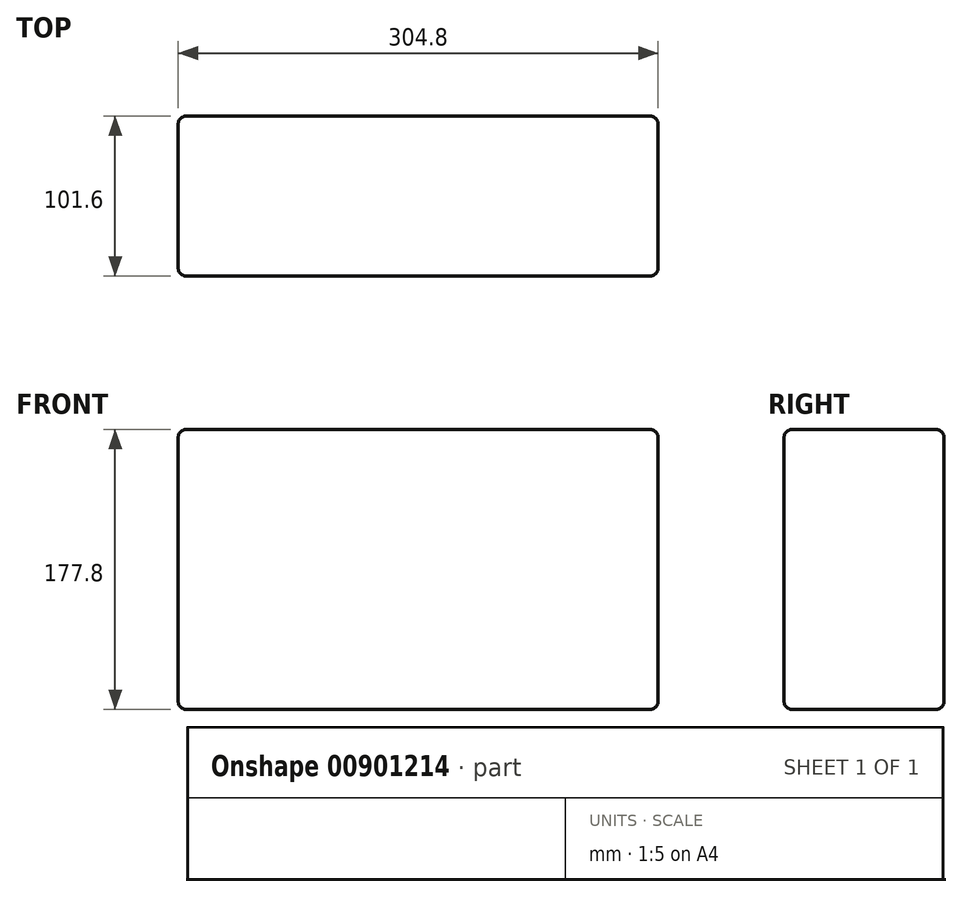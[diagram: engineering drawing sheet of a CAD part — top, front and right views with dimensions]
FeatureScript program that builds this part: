
annotation { "Feature Type Name" : "Feature", "Feature Type Description" : "" }
export const myFeature = defineFeature(function(context is Context, id is Id, definition is map)
    precondition{}
    {
        {
            var Q0;
            Q0=qCreatedBy(makeId("Front.planeOp"),FACE);
            var sketch = newSketch(context, id + "F0", { "sketchPlane" : qUnion([Q0])});
            skLineSegment(sketch, "E0.bottom", {"start": v(-304.8, 177.8) * mm, "end": v(0, 177.8) * mm});
            skLineSegment(sketch, "E0.top", {"start": v(-304.8, 0) * mm, "end": v(0, 0) * mm});
            skLineSegment(sketch, "E0.left", {"start": v(-304.8, 177.8) * mm, "end": v(-304.8, 0) * mm});
            skLineSegment(sketch, "E0.right", {"start": v(0, 177.8) * mm, "end": v(0, 0) * mm});
            skSolve(sketch);
        }
        {
            var Q0;
            Q0=makeQuery(id+"F0.imprint","IMPRINT",FACE,{"disambiguationData":[TD([[makeQuery(id+"F0.imprint","IMPRINT",EDGE,{"derivedFrom":sQuery(id+"F0.wireOp",EDGE,"E0.bottom")}),-1.0]])]});
            extrude(context, id + "F1", {"entities" : qUnion([Q0]), "depth" : 101.6 * mm, "offsetDistance" : 25.4 * mm});
        }
        {
            var Q0;
            Q0=makeQuery(id+"F1.opExtrude","SWEPT_EDGE",EDGE,{"disambiguationData":[OSD([sQuery(id+"F0.wireOp",EDGE,"E0.bottom"),sQuery(id+"F0.wireOp",EDGE,"E0.left")])]});
            var Q1;
            Q1=makeQuery(id+"F1.opExtrude","SWEPT_FACE",FACE,{"disambiguationData":[OSD([sQuery(id+"F0.wireOp",EDGE,"E0.bottom")])]});
            var Q2;
            Q2=makeQuery(id+"F1.opExtrude","SWEPT_EDGE",EDGE,{"disambiguationData":[OSD([sQuery(id+"F0.wireOp",EDGE,"E0.bottom"),sQuery(id+"F0.wireOp",EDGE,"E0.right")])]});
            var Q3;
            Q3=makeQuery(id+"F1.opExtrude","CAP_FACE",FACE,{"disambiguationData":[OSD([sQuery(id+"F0.wireOp",EDGE,"E0.bottom"),sQuery(id+"F0.wireOp",EDGE,"E0.top"),sQuery(id+"F0.wireOp",EDGE,"E0.left"),sQuery(id+"F0.wireOp",EDGE,"E0.right")])],"isStart":true});
            var Q4;
            Q4=makeQuery(id+"F1.opExtrude","CAP_FACE",FACE,{"disambiguationData":[OSD([sQuery(id+"F0.wireOp",EDGE,"E0.bottom"),sQuery(id+"F0.wireOp",EDGE,"E0.top"),sQuery(id+"F0.wireOp",EDGE,"E0.left"),sQuery(id+"F0.wireOp",EDGE,"E0.right")])],"isStart":false});
            var Q5;
            Q5=makeQuery(id+"F1.opExtrude","SWEPT_EDGE",EDGE,{"disambiguationData":[OSD([sQuery(id+"F0.wireOp",EDGE,"E0.top"),sQuery(id+"F0.wireOp",EDGE,"E0.right")])]});
            var Q6;
            Q6=makeQuery(id+"F1.opExtrude","SWEPT_FACE",FACE,{"disambiguationData":[OSD([sQuery(id+"F0.wireOp",EDGE,"E0.top")])]});
            var Q7;
            Q7=makeQuery(id+"F1.opExtrude","CAP_EDGE",EDGE,{"disambiguationData":[OSD([sQuery(id+"F0.wireOp",EDGE,"E0.bottom")])],"isStart":true});
            var Q8;
            Q8=makeQuery(id+"F1.opExtrude","CAP_EDGE",EDGE,{"disambiguationData":[OSD([sQuery(id+"F0.wireOp",EDGE,"E0.bottom")])],"isStart":false});
            var Q9;
            Q9=makeQuery(id+"F1.opExtrude","SWEPT_FACE",FACE,{"disambiguationData":[OSD([sQuery(id+"F0.wireOp",EDGE,"E0.right")])]});
            var Q10;
            Q10=makeQuery(id+"F1.opExtrude","CAP_EDGE",EDGE,{"disambiguationData":[OSD([sQuery(id+"F0.wireOp",EDGE,"E0.top")])],"isStart":false});
            var Q11;
            Q11=makeQuery(id+"F1.opExtrude","SWEPT_EDGE",EDGE,{"disambiguationData":[OSD([sQuery(id+"F0.wireOp",EDGE,"E0.top"),sQuery(id+"F0.wireOp",EDGE,"E0.left")])]});
            var Q12;
            Q12=makeQuery(id+"F1.opExtrude","SWEPT_FACE",FACE,{"disambiguationData":[OSD([sQuery(id+"F0.wireOp",EDGE,"E0.left")])]});
            var Q13;
            Q13=makeQuery(id+"F1.opExtrude","CAP_EDGE",EDGE,{"disambiguationData":[OSD([sQuery(id+"F0.wireOp",EDGE,"E0.top")])],"isStart":true});
            var Q14;
            Q14=makeQuery(id+"F1.opExtrude","CAP_EDGE",EDGE,{"disambiguationData":[OSD([sQuery(id+"F0.wireOp",EDGE,"E0.left")])],"isStart":true});
            var Q15;
            Q15=makeQuery(id+"F1.opExtrude","CAP_EDGE",EDGE,{"disambiguationData":[OSD([sQuery(id+"F0.wireOp",EDGE,"E0.left")])],"isStart":false});
            var Q16;
            Q16=makeQuery(id+"F1.opExtrude","CAP_EDGE",EDGE,{"disambiguationData":[OSD([sQuery(id+"F0.wireOp",EDGE,"E0.right")])],"isStart":true});
            var Q17;
            Q17=makeQuery(id+"F1.opExtrude","CAP_EDGE",EDGE,{"disambiguationData":[OSD([sQuery(id+"F0.wireOp",EDGE,"E0.right")])],"isStart":false});
            fillet(context, id + "F2", {"entities" : qUnion([Q0, Q1, Q2, Q3, Q4, Q5, Q6, Q7, Q8, Q9, Q10, Q11, Q12, Q13, Q14, Q15, Q16, Q17]), "radius" : 5.08 * mm, "tangentPropagation" : true, "allowEdgeOverflow" : false});
        }
    });
